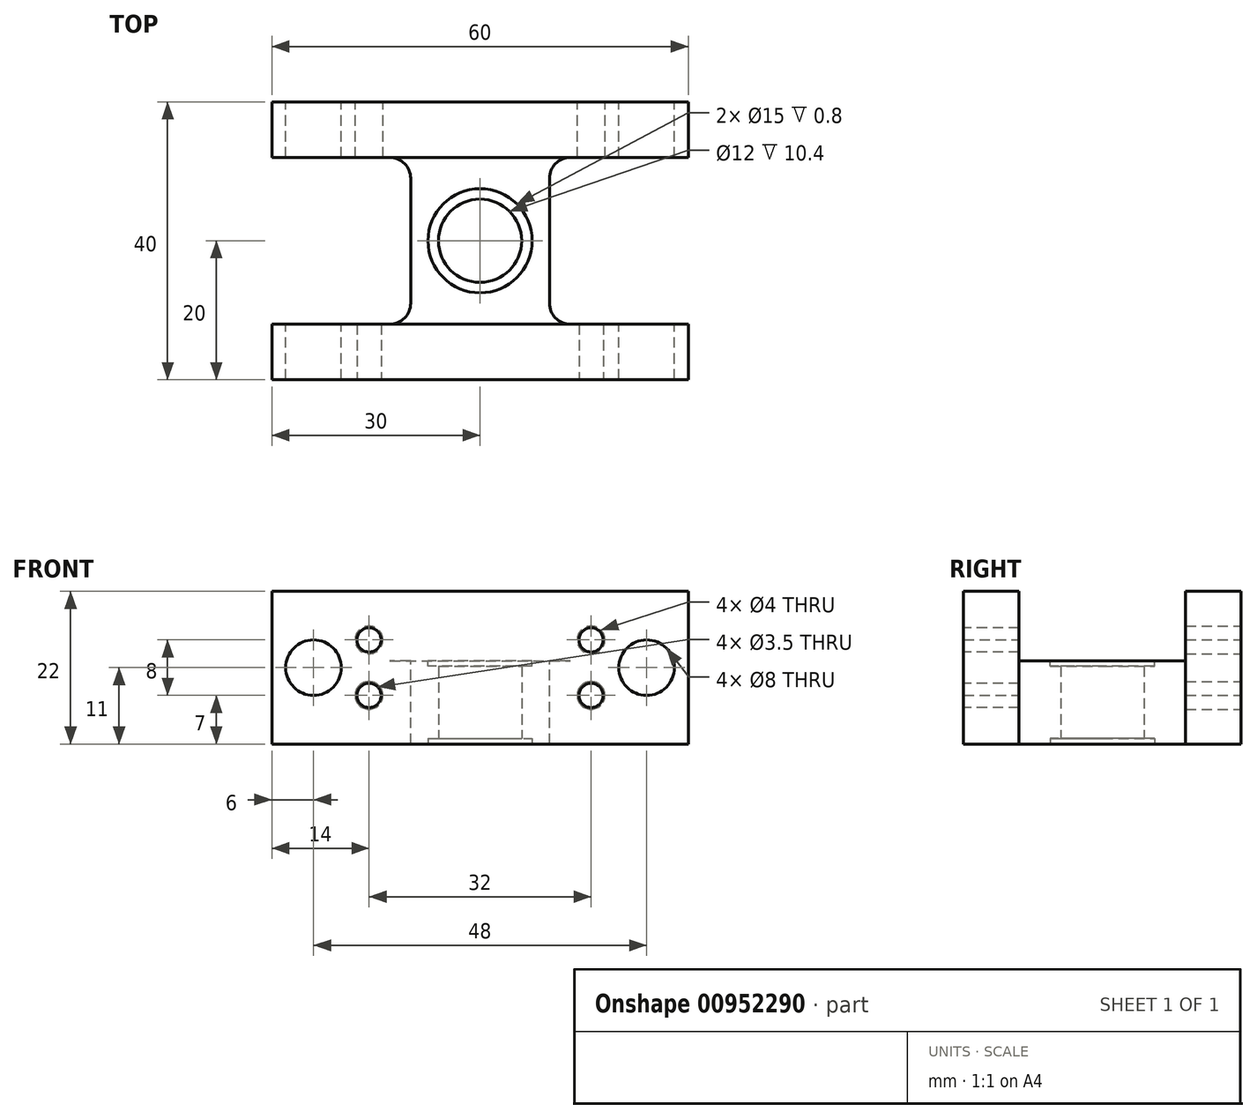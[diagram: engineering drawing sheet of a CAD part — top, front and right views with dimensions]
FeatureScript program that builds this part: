
annotation { "Feature Type Name" : "Feature", "Feature Type Description" : "" }
export const myFeature = defineFeature(function(context is Context, id is Id, definition is map)
    precondition{}
    {
        {
            var Q0;
            Q0=qCreatedBy(makeId("Top.planeOp"),FACE);
            var sketch = newSketch(context, id + "F0", { "sketchPlane" : qUnion([Q0])});
            skLineSegment(sketch, "E0.bottom", {"start": v(30, -20) * mm, "end": v(-30, -20) * mm});
            skLineSegment(sketch, "E0.top", {"start": v(30, 20) * mm, "end": v(-30, 20) * mm});
            skLineSegment(sketch, "E0.left", {"start": v(30, -20) * mm, "end": v(30, 20) * mm});
            skLineSegment(sketch, "E0.right", {"start": v(-30, -20) * mm, "end": v(-30, 20) * mm});
            skPoint(sketch, "E0.middle", {"position": v(0, 0) * mm});
            skCircle(sketch, "E1", {"center": v(0, 0) * mm, "radius": 6 * mm});
            skSolve(sketch);
        }
        {
            var Q0;
            Q0=qSketchRegion(id+"F0",true);
            extrude(context, id + "F1", {"entities" : qUnion([Q0]), "depth" : 12 * mm, "offsetDistance" : 25 * mm, "symmetric" : true});
        }
        {
            var Q0;
            Q0=makeQuery(id+"F1.opExtrude","SWEPT_FACE",FACE,{"disambiguationData":[OSD([sQuery(id+"F0.wireOp",EDGE,"E0.left")])]});
            var sketch = newSketch(context, id + "F2", { "sketchPlane" : qUnion([Q0])});
            skLineSegment(sketch, "E2.bottom", {"start": v(20, 6) * mm, "end": v(12, 6) * mm});
            skLineSegment(sketch, "E2.top", {"start": v(20, 16) * mm, "end": v(12, 16) * mm});
            skLineSegment(sketch, "E2.left", {"start": v(20, 6) * mm, "end": v(20, 16) * mm});
            skLineSegment(sketch, "E2.right", {"start": v(12, 6) * mm, "end": v(12, 16) * mm});
            skLineSegment(sketch, "E3.MirrorCS", {"start": v(-12, 6) * mm, "end": v(-12, 16) * mm});
            skLineSegment(sketch, "E4.MirrorCS", {"start": v(-20, 16) * mm, "end": v(-12, 16) * mm});
            skLineSegment(sketch, "E5.MirrorCS", {"start": v(-20, 6) * mm, "end": v(-20, 16) * mm});
            skSolve(sketch);
        }
        {
            var Q0;
            Q0=qSketchRegion(id+"F2",true);
            var Q1;
            {var subQ0=sQuery(id+"F2.wireOp",EDGE,"E3.MirrorCS");Q1=makeQuery(id+"F2.imprint","IMPRINT",FACE,{"disambiguationData":[TD([[makeQuery(id+"F2.imprint","IMPRINT",EDGE,{"derivedFrom":subQ0}),1.0]])]});}
            var Q2;
            Q2=makeQuery(id+"F1.opExtrude","SWEPT_FACE",FACE,{"disambiguationData":[OSD([sQuery(id+"F0.wireOp",EDGE,"E0.right")])]});
            extrude(context, id + "F3", {"entities" : qUnion([Q0, Q1]), "operationType" : NewBodyOperationType.ADD, "endBound" : BoundingType.UP_TO_SURFACE, "oppositeDirection" : true, "depth" : 25 * mm, "endBoundEntityFace" : qUnion([Q2]), "offsetDistance" : 25 * mm});
        }
        {
            var Q0;
            Q0=makeQuery(id+"F3.boolean.opBoolean","MERGE",FACE,{"derivedFrom":[makeQuery(id+"F1.opExtrude","SWEPT_FACE",FACE,{"disambiguationData":[OSD([sQuery(id+"F0.wireOp",EDGE,"E0.top")])]}),makeQuery(id+"F3.opExtrude","SWEPT_FACE",FACE,{"disambiguationData":[OSD([sQuery(id+"F2.wireOp",EDGE,"E2.left")])]})]});
            var sketch = newSketch(context, id + "F4", { "sketchPlane" : qUnion([Q0])});
            skCircle(sketch, "E6", {"center": v(16, 9) * mm, "radius": 2 * mm});
            skCircle(sketch, "E7.MirrorC", {"center": v(-16, 9) * mm, "radius": 2 * mm});
            skLineSegment(sketch, "E8", {"start": v(30, 5) * mm, "end": v(17.34, 5) * mm});
            skCircle(sketch, "E9.MirrorC", {"center": v(16, 1) * mm, "radius": 2 * mm});
            skCircle(sketch, "E10.MirrorC", {"center": v(-16, 1) * mm, "radius": 2 * mm});
            skSolve(sketch);
        }
        {
            var Q0;
            Q0=qSketchRegion(id+"F4",true);
            var Q1;
            Q1=makeQuery(id+"F3.opExtrude","SWEPT_FACE",FACE,{"disambiguationData":[OSD([sQuery(id+"F2.wireOp",EDGE,"E2.right")])]});
            extrude(context, id + "F5", {"entities" : qUnion([Q0]), "operationType" : NewBodyOperationType.REMOVE, "oppositeDirection" : true, "depth" : 10 * mm, "endBoundEntityFace" : qUnion([Q1]), "offsetDistance" : 25 * mm});
        }
        {
            var Q0;
            Q0=makeQuery(id+"F3.boolean.opBoolean","MERGE",FACE,{"derivedFrom":[makeQuery(id+"F1.opExtrude","SWEPT_FACE",FACE,{"disambiguationData":[OSD([sQuery(id+"F0.wireOp",EDGE,"E0.bottom")])]}),makeQuery(id+"F3.opExtrude","SWEPT_FACE",FACE,{"disambiguationData":[OSD([sQuery(id+"F2.wireOp",EDGE,"E5.MirrorCS")])]})]});
            var sketch = newSketch(context, id + "F6", { "sketchPlane" : qUnion([Q0])});
            skCircle(sketch, "E11", {"center": v(16, 9) * mm, "radius": 1.75 * mm});
            skCircle(sketch, "E12.MirrorC", {"center": v(-16, 9) * mm, "radius": 1.75 * mm});
            skLineSegment(sketch, "E13", {"start": v(30, 5) * mm, "end": v(18.29, 5) * mm});
            skCircle(sketch, "E14.MirrorC", {"center": v(16, 1) * mm, "radius": 1.75 * mm});
            skCircle(sketch, "E15.MirrorC", {"center": v(-16, 1) * mm, "radius": 1.75 * mm});
            skSolve(sketch);
        }
        {
            var Q0;
            Q0=qSketchRegion(id+"F6",true);
            var Q1;
            Q1=makeQuery(id+"F3.opExtrude","SWEPT_FACE",FACE,{"disambiguationData":[OSD([sQuery(id+"F2.wireOp",EDGE,"E3.MirrorCS")])]});
            extrude(context, id + "F7", {"entities" : qUnion([Q0]), "operationType" : NewBodyOperationType.REMOVE, "oppositeDirection" : true, "depth" : 10 * mm, "endBoundEntityFace" : qUnion([Q1]), "offsetDistance" : 25 * mm});
        }
        {
            var Q0;
            Q0=makeQuery(id+"F1.opExtrude","CAP_FACE",FACE,{"disambiguationData":[OSD([sQuery(id+"F0.wireOp",EDGE,"E0.bottom"),sQuery(id+"F0.wireOp",EDGE,"E0.top"),sQuery(id+"F0.wireOp",EDGE,"E0.left"),sQuery(id+"F0.wireOp",EDGE,"E0.right"),sQuery(id+"F0.wireOp",EDGE,"E1")])],"isStart":false});
            var sketch = newSketch(context, id + "F8", { "sketchPlane" : qUnion([Q0])});
            skCircle(sketch, "E16", {"center": v(0, 0) * mm, "radius": 7.5 * mm});
            skSolve(sketch);
        }
        {
            var Q0;
            Q0=qSketchRegion(id+"F8",true);
            extrude(context, id + "F9", {"entities" : qUnion([Q0]), "operationType" : NewBodyOperationType.REMOVE, "oppositeDirection" : true, "depth" : 0.8 * mm, "offsetDistance" : 25 * mm});
        }
        {
            var Q0;
            Q0=makeQuery(id+"F1.opExtrude","CAP_FACE",FACE,{"disambiguationData":[OSD([sQuery(id+"F0.wireOp",EDGE,"E0.bottom"),sQuery(id+"F0.wireOp",EDGE,"E0.top"),sQuery(id+"F0.wireOp",EDGE,"E0.left"),sQuery(id+"F0.wireOp",EDGE,"E0.right"),sQuery(id+"F0.wireOp",EDGE,"E1")])],"isStart":true});
            var sketch = newSketch(context, id + "F10", { "sketchPlane" : qUnion([Q0])});
            skCircle(sketch, "E17", {"center": v(0, 0) * mm, "radius": 7.5 * mm});
            skSolve(sketch);
        }
        {
            var Q0;
            Q0=qSketchRegion(id+"F10",true);
            extrude(context, id + "F11", {"entities" : qUnion([Q0]), "operationType" : NewBodyOperationType.REMOVE, "oppositeDirection" : true, "depth" : 0.8 * mm, "offsetDistance" : 25 * mm});
        }
        {
            var Q0;
            Q0=makeQuery(id+"F1.opExtrude","CAP_FACE",FACE,{"disambiguationData":[OSD([sQuery(id+"F0.wireOp",EDGE,"E0.bottom"),sQuery(id+"F0.wireOp",EDGE,"E0.top"),sQuery(id+"F0.wireOp",EDGE,"E0.left"),sQuery(id+"F0.wireOp",EDGE,"E0.right"),sQuery(id+"F0.wireOp",EDGE,"E1")])],"isStart":false});
            var sketch = newSketch(context, id + "F12", { "sketchPlane" : qUnion([Q0])});
            skLineSegment(sketch, "E18.bottom", {"start": v(10, 12) * mm, "end": v(30, 12) * mm});
            skLineSegment(sketch, "E18.top", {"start": v(10, -12) * mm, "end": v(30, -12) * mm});
            skLineSegment(sketch, "E18.left", {"start": v(10, 12) * mm, "end": v(10, -12) * mm});
            skLineSegment(sketch, "E18.right", {"start": v(30, 12) * mm, "end": v(30, -12) * mm});
            skLineSegment(sketch, "E19.MirrorCS", {"start": v(-10, 12) * mm, "end": v(-10, -12) * mm});
            skLineSegment(sketch, "E20.MirrorCS", {"start": v(-10, 12) * mm, "end": v(-30, 12) * mm});
            skLineSegment(sketch, "E21.MirrorCS", {"start": v(-30, 12) * mm, "end": v(-30, -12) * mm});
            skLineSegment(sketch, "E22.MirrorCS", {"start": v(-10, -12) * mm, "end": v(-30, -12) * mm});
            skSolve(sketch);
        }
        {
            var Q0;
            Q0 = qSketchRegion(id + "F12", true);
            extrude(context, id + "F13", {"entities" : qUnion([Q0]), "operationType" : NewBodyOperationType.REMOVE, "oppositeDirection" : true, "depth" : 25 * mm, "offsetDistance" : 25 * mm});
        }
        {
            var Q0;
            Q0=makeQuery(id+"F13.boolean.opBoolean","COPY",EDGE,{"derivedFrom":makeQuery(id+"F13.opExtrude","SWEPT_EDGE",EDGE,{"disambiguationData":[OSD([sQuery(id+"F0.wireOp",EDGE,"E0.left"),sQuery(id+"F2.wireOp",EDGE,"E2.bottom"),sQuery(id+"F2.wireOp",EDGE,"E2.right"),sQuery(id+"F12.wireOp",EDGE,"E19.MirrorCS"),sQuery(id+"F12.wireOp",EDGE,"E20.MirrorCS")])]})});
            var Q1;
            Q1=makeQuery(id+"F13.boolean.opBoolean","COPY",EDGE,{"derivedFrom":makeQuery(id+"F13.opExtrude","SWEPT_EDGE",EDGE,{"disambiguationData":[OSD([sQuery(id+"F0.wireOp",EDGE,"E0.left"),sQuery(id+"F2.wireOp",EDGE,"E2.bottom"),sQuery(id+"F2.wireOp",EDGE,"E2.right"),sQuery(id+"F12.wireOp",EDGE,"E18.bottom"),sQuery(id+"F12.wireOp",EDGE,"E18.left")])]})});
            var Q2;
            Q2=makeQuery(id+"F13.boolean.opBoolean","COPY",EDGE,{"derivedFrom":makeQuery(id+"F13.opExtrude","SWEPT_EDGE",EDGE,{"disambiguationData":[OSD([sQuery(id+"F0.wireOp",EDGE,"E0.left"),sQuery(id+"F2.wireOp",EDGE,"E3.MirrorCS"),sQuery(id+"F12.wireOp",EDGE,"E18.top"),sQuery(id+"F12.wireOp",EDGE,"E18.left")])]})});
            var Q3;
            Q3=makeQuery(id+"F13.boolean.opBoolean","COPY",EDGE,{"derivedFrom":makeQuery(id+"F13.opExtrude","SWEPT_EDGE",EDGE,{"disambiguationData":[OSD([sQuery(id+"F0.wireOp",EDGE,"E0.left"),sQuery(id+"F2.wireOp",EDGE,"E3.MirrorCS"),sQuery(id+"F12.wireOp",EDGE,"E19.MirrorCS"),sQuery(id+"F12.wireOp",EDGE,"E22.MirrorCS")])]})});
            fillet(context, id + "F14", {"entities" : qUnion([Q0, Q1, Q2, Q3]), "tangentPropagation" : true, "radius" : 3 * mm, "defaultsChanged" : true, "vertexSettings" : [], "allowEdgeOverflow" : false});
        }
        {
            var Q0;
            Q0=makeQuery(id+"F3.boolean.opBoolean","MERGE",FACE,{"derivedFrom":[makeQuery(id+"F1.opExtrude","SWEPT_FACE",FACE,{"disambiguationData":[OSD([sQuery(id+"F0.wireOp",EDGE,"E0.top")])]}),makeQuery(id+"F3.opExtrude","SWEPT_FACE",FACE,{"disambiguationData":[OSD([sQuery(id+"F2.wireOp",EDGE,"E2.left")])]})]});
            var sketch = newSketch(context, id + "F15", { "sketchPlane" : qUnion([Q0])});
            skCircle(sketch, "E23", {"center": v(24, 5) * mm, "radius": 4 * mm});
            skPoint(sketch, "E23.centerSnap0", {"position": v(30, 5) * mm});
            skCircle(sketch, "E24.MirrorC", {"center": v(-24, 5) * mm, "radius": 4 * mm});
            skSolve(sketch);
        }
        {
            var Q0;
            Q0 = qSketchRegion(id + "F15", true);
            extrude(context, id + "F16", {"entities" : qUnion([Q0]), "operationType" : NewBodyOperationType.REMOVE, "endBound" : BoundingType.THROUGH_ALL, "oppositeDirection" : true, "depth" : 25 * mm, "offsetDistance" : 25 * mm});
        }
    });
